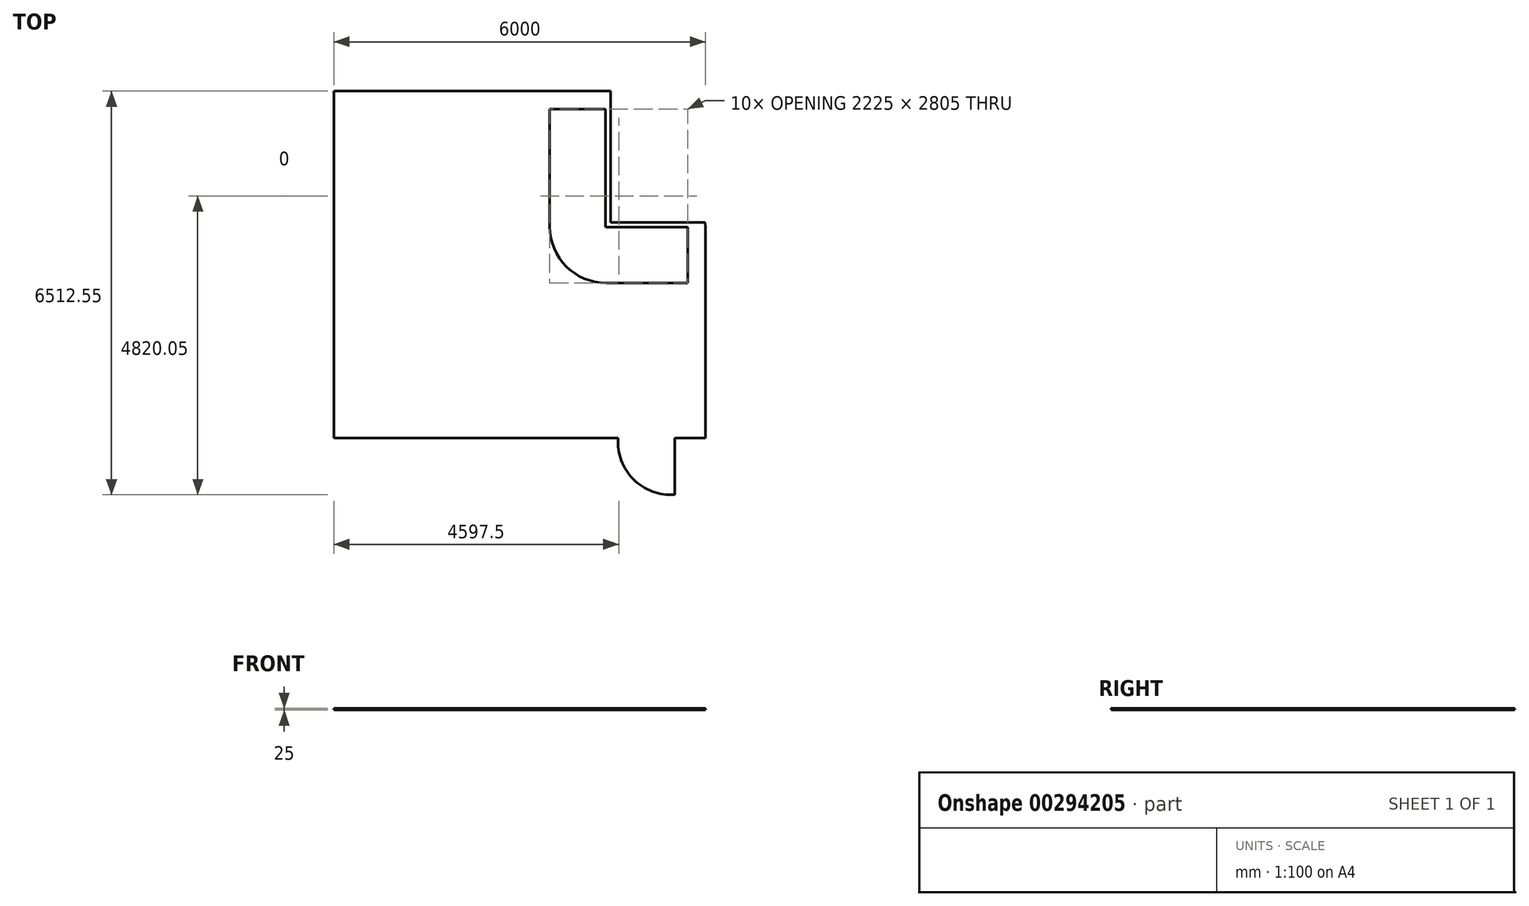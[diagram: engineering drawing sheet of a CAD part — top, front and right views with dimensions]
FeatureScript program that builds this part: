
annotation { "Feature Type Name" : "Feature", "Feature Type Description" : "" }
export const myFeature = defineFeature(function(context is Context, id is Id, definition is map)
    precondition{}
    {
        {
            var Q0;
            Q0=qCreatedBy(makeId("Top.planeOp"),FACE);
            var sketch = newSketch(context, id + "F0", { "sketchPlane" : qUnion([Q0])});
            skLineSegment(sketch, "E0", {"start": v(-3423.66, 2854.9) * mm, "end": v(-3423.66, -2745.1) * mm});
            skLineSegment(sketch, "E1", {"start": v(-3423.66, 2854.9) * mm, "end": v(61.34, 2854.9) * mm});
            skLineSegment(sketch, "E2", {"start": v(61.34, 2854.9) * mm, "end": v(61.34, 669.9) * mm});
            skLineSegment(sketch, "E3", {"start": v(971.34, -240.1) * mm, "end": v(2576.34, -240.1) * mm});
            skLineSegment(sketch, "E4", {"start": v(-3423.66, -2745.1) * mm, "end": v(1166.34, -2745.1) * mm});
            skLineSegment(sketch, "E5", {"start": v(2576.34, -240.1) * mm, "end": v(2576.34, -2745.1) * mm});
            skLineSegment(sketch, "E6", {"start": v(2576.34, -2745.1) * mm, "end": v(2076.34, -2745.1) * mm});
            skLineSegment(sketch, "E7", {"start": v(61.34, 2854.9) * mm, "end": v(961.34, 2854.9) * mm});
            skLineSegment(sketch, "E8", {"start": v(2576.34, -240.1) * mm, "end": v(2576.34, 659.9) * mm});
            skLineSegment(sketch, "E9", {"start": v(961.34, 2854.9) * mm, "end": v(961.34, 659.9) * mm});
            skLineSegment(sketch, "E10", {"start": v(2576.34, 659.9) * mm, "end": v(961.34, 659.9) * mm});
            skLineSegment(sketch, "E11", {"start": v(61.34, 2854.9) * mm, "end": v(511.34, 2854.9) * mm});
            skLineSegment(sketch, "E12", {"start": v(511.34, 2854.9) * mm, "end": v(511.34, 2996.9) * mm});
            skLineSegment(sketch, "E13", {"start": v(511.34, 2854.9) * mm, "end": v(511.34, 664.9) * mm});
            skLineSegment(sketch, "E14", {"start": v(966.34, 209.9) * mm, "end": v(2576.34, 209.9) * mm});
            skLineSegment(sketch, "E15", {"start": v(2576.34, 209.9) * mm, "end": v(2576.34, 659.9) * mm});
            skLineSegment(sketch, "E16", {"start": v(61.34, 2564.9) * mm, "end": v(961.34, 2564.9) * mm});
            skLineSegment(sketch, "E17", {"start": v(961.34, 2564.9) * mm, "end": v(961.34, 2274.9) * mm});
            skLineSegment(sketch, "E18", {"start": v(961.34, 2274.9) * mm, "end": v(61.34, 2274.9) * mm});
            skLineSegment(sketch, "E19", {"start": v(61.34, 1984.9) * mm, "end": v(961.34, 1984.9) * mm});
            skLineSegment(sketch, "E20", {"start": v(961.34, 1984.9) * mm, "end": v(961.34, 1694.9) * mm});
            skLineSegment(sketch, "E21", {"start": v(961.34, 1694.9) * mm, "end": v(61.34, 1694.9) * mm});
            skLineSegment(sketch, "E22", {"start": v(61.34, 1694.9) * mm, "end": v(61.34, 1404.9) * mm});
            skLineSegment(sketch, "E23", {"start": v(61.34, 1404.9) * mm, "end": v(961.34, 1404.9) * mm});
            skLineSegment(sketch, "E24", {"start": v(961.34, 1404.9) * mm, "end": v(961.34, 1114.9) * mm});
            skLineSegment(sketch, "E25", {"start": v(61.34, 1114.9) * mm, "end": v(961.34, 1114.9) * mm});
            skLineSegment(sketch, "E26", {"start": v(2286.34, 659.9) * mm, "end": v(2286.34, -240.1) * mm});
            skLineSegment(sketch, "E27", {"start": v(1996.34, -240.1) * mm, "end": v(1996.34, 659.9) * mm});
            skPoint(sketch, "E28.orphan", {"position": v(1768.84, 659.9) * mm});
            skPoint(sketch, "E29.end.orphan", {"position": v(1768.84, -240.1) * mm});
            skLineSegment(sketch, "E30", {"start": v(1706.34, 659.9) * mm, "end": v(1706.34, -240.1) * mm});
            skLineSegment(sketch, "E31", {"start": v(1416.34, -240.1) * mm, "end": v(1416.34, 659.9) * mm});
            skLineSegment(sketch, "E32", {"start": v(2076.34, -2827.61) * mm, "end": v(2076.34, -2745.1) * mm});
            skLineSegment(sketch, "E33", {"start": v(2076.34, -2745.1) * mm, "end": v(2076.34, -3655.1) * mm});
            skArc(sketch, "E34", {"start": v(1166.34, -2745.1) * mm, "mid": v(1411.87, -3409.56) * mm, "end": v(2076.34, -3655.1) * mm});
            skLineSegment(sketch, "E35.trimOffspring", {"start": v(2076.34, -2745.1) * mm, "end": v(2576.34, -2745.1) * mm});
            skPoint(sketch, "E36.visualSharp", {"position": v(61.34, -240.1) * mm});
            skArc(sketch, "E36.filletArc", {"start": v(61.34, 669.9) * mm, "mid": v(327.87, 26.44) * mm, "end": v(971.34, -240.1) * mm});
            skPoint(sketch, "E37.visualSharp", {"position": v(511.34, 209.9) * mm});
            skArc(sketch, "E37.filletArc", {"start": v(511.34, 664.9) * mm, "mid": v(644.6, 343.17) * mm, "end": v(966.34, 209.9) * mm});
            skLineSegment(sketch, "E38", {"start": v(961.34, 2854.9) * mm, "end": v(1041.34, 2854.9) * mm});
            skLineSegment(sketch, "E39", {"start": v(1041.34, 2854.9) * mm, "end": v(1041.34, 739.63) * mm});
            skLineSegment(sketch, "E40", {"start": v(2569.72, 739.63) * mm, "end": v(2576.34, 659.9) * mm});
            skLineSegment(sketch, "E41", {"start": v(2569.72, 739.63) * mm, "end": v(1041.34, 739.63) * mm});
            skSolve(sketch);
        }
        {
            var Q0;
            Q0 = qSketchRegion(id + "F0", true);
            extrude(context, id + "F1", {"entities" : qUnion([Q0]), "depth" : 25 * mm});
        }
    });
